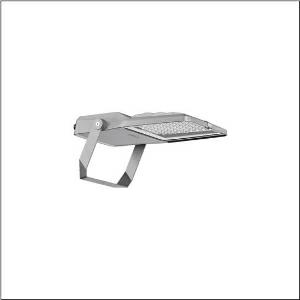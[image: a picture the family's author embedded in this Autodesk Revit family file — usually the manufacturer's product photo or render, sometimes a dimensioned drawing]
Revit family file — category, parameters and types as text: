
# Revit family: floodlight_fl_21_mini___pl43_5xa7774c2a1a_b50a
name_source: partatom
category: Lighting Fixtures
units: mm (PartAtom-declared; Revit-internal decimal feet)

## family parameters
Cut with Voids When Loaded = No
Host = Face
Light Source = No
Part Type = Normal
Room Calculation Point = No
Round Connector Dimension = Use Diameter
Shared = No

## types (1)
- --- (1 x LED, 12480 lm, 88.8 W, 3000K)
    Apparent Load = 89 VA
    CIE Flux Codes = 27 78 99 100 100
    Color Rendering = 70
    Color Temperature = 3000K
    Default Elevation = 1800 mm
    Description = Floodlight FL 21 mini, floodlight, primary light control with lens, of PMMA, primary optical cover: protective disc, of toughened safety glass, transparent, light distribution: PL43, light emission: direct distribution, installation type: surface-mounted, LED, High Power LED, rated luminous flux: 12.480lm, luminous efficacy: 141lm/W, light colour: 730, colour temperature: 3000K, control gear: DALI 2, control: overheat protection, power reduction, constant luminous flux control, flexible luminous flux parameterisation, pre-setting: linear dimming characteristic, with terminal, 6-pole, mains connection: 220..240V, AC/DC, 0/50..60Hz, start of lifetime: 89W, end of service life: 94W, reduction: 42W, luminaire housing, of diecast aluminium, powder-coated, SITECO metallic grey (DB 702S), corrosivity category C5 mid according to DIN EN ISO 12944, chlorine-resistant, suitable for swimming pools, sealing non-destructively replaceable, mounting bracket, of steel, galvanised, powder-coated, SITECO metallic grey (DB 702S), protection rating (complete): IP66, insulation class (complete): insulation class II (safety insulation), certification: CE, ENEC, VDE, impact resistance: IK08, permissible operating ambient temperature: -40..+40°C, permissible operating ambient temperature for outdoor applications: -40..+50°C, standard: DIN EN 12944, LABS conformity tested according to VDMA 24364:2018-05, packaging unit: 1 piece

Light Distribution: PL43
    Height = 70 mm
    Lamp = 1 x LED
    Lamp Light Flux = 12480 lm
    Lamp Power = 88.8 W
    Lamp count = 1
    Length = 485 mm
    Luminous efficacy = 141 lm/W
    Manufacturer = Siteco
    ModVariant = No
    Model = 5XA7774C2A1A
    Number of Poles = 1
    OnlyDefault = Yes
    Power Factor = 1
    Product Name = Floodlight FL 21 mini | PL43
    Product group = floodlight | pylon annexe
    ProductGroupID = 6201
    Protection Class = Protection class II
    Protection Degree = IP 66
    RLX_Detail_Level = 1
    RLX_Emergency_Light_Flux = 0 lm
    RLX_Emergency_Type = 0
    RLX_Emergency_Type_DB = No
    RlxData = <blob elided: 95869 chars, md5=a10c17f7>
    Socket = socket
    Standby Power = 0 W
    System Light Flux = 12480 lm
    System Power = 89 W
    Type Comments = factory setting: luminous flux: 100 % | dim-lin: 254 | 456 mA
    Type Image = l_1006845.jpg
    URL = http://relux.com
    VarID = @adj_161695
    Voltage = 0 V
    Weight = 0.00 kg
    Width = 337 mm

## geometry (parser evidence)
native form markers: Blend x4, Sweep x11
no freeform markers — native parametric forms only
